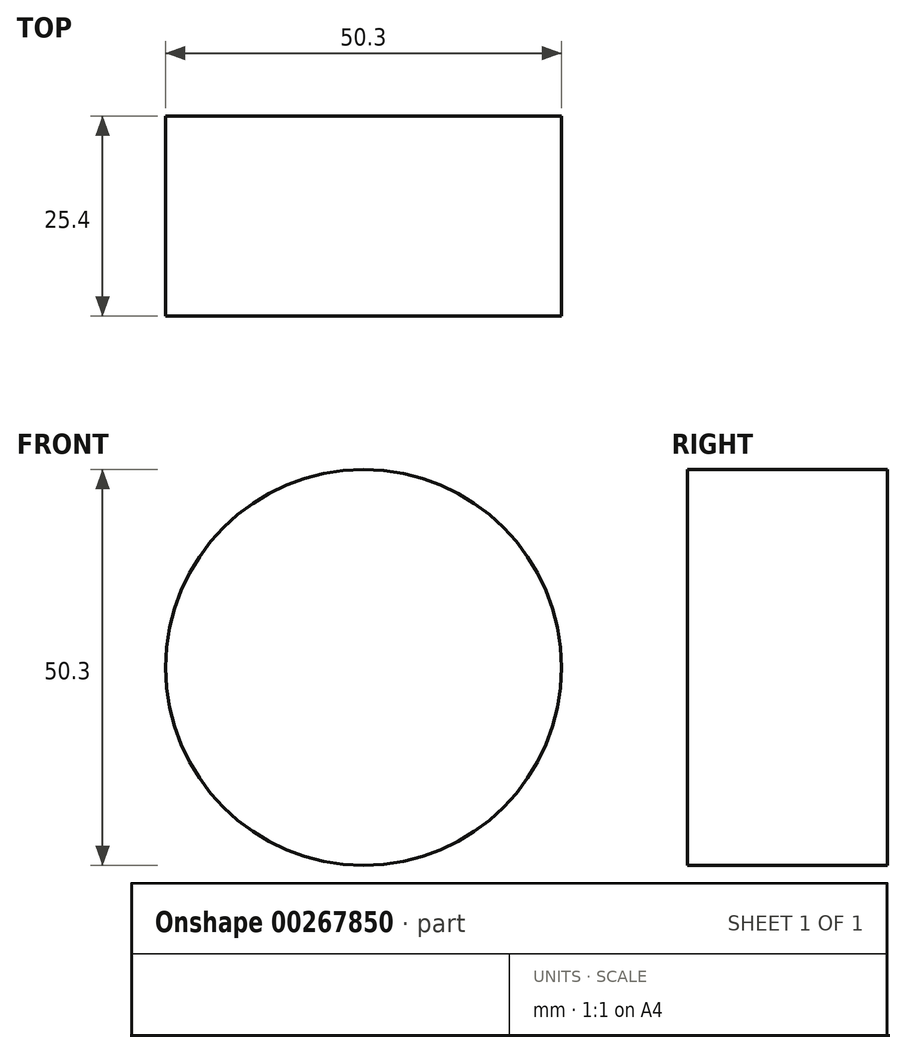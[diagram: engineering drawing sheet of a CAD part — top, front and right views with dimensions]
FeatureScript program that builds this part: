
annotation { "Feature Type Name" : "Feature", "Feature Type Description" : "" }
export const myFeature = defineFeature(function(context is Context, id is Id, definition is map)
    precondition{}
    {
        {
            var Q0;
            Q0=qCreatedBy(makeId("Front.planeOp"),FACE);
            var sketch = newSketch(context, id + "F0", { "sketchPlane" : qUnion([Q0])});
            skCircle(sketch, "E0", {"center": v(-23.4, 20.34) * mm, "radius": 25.23 * mm});
            skCircle(sketch, "E1", {"center": v(-23.4, 20.34) * mm, "radius": 25.15 * mm});
            skSolve(sketch);
        }
        {
            var Q0;
            Q0=makeQuery(id+"F0.imprint","IMPRINT",FACE,{"disambiguationData":[TD([[makeQuery(id+"F0.imprint","IMPRINT",EDGE,{"derivedFrom":sQuery(id+"F0.wireOp",EDGE,"E1")}),1.0]])]});
            extrude(context, id + "F1", {"entities" : qUnion([Q0]), "depth" : 25.4 * mm});
        }
    });
